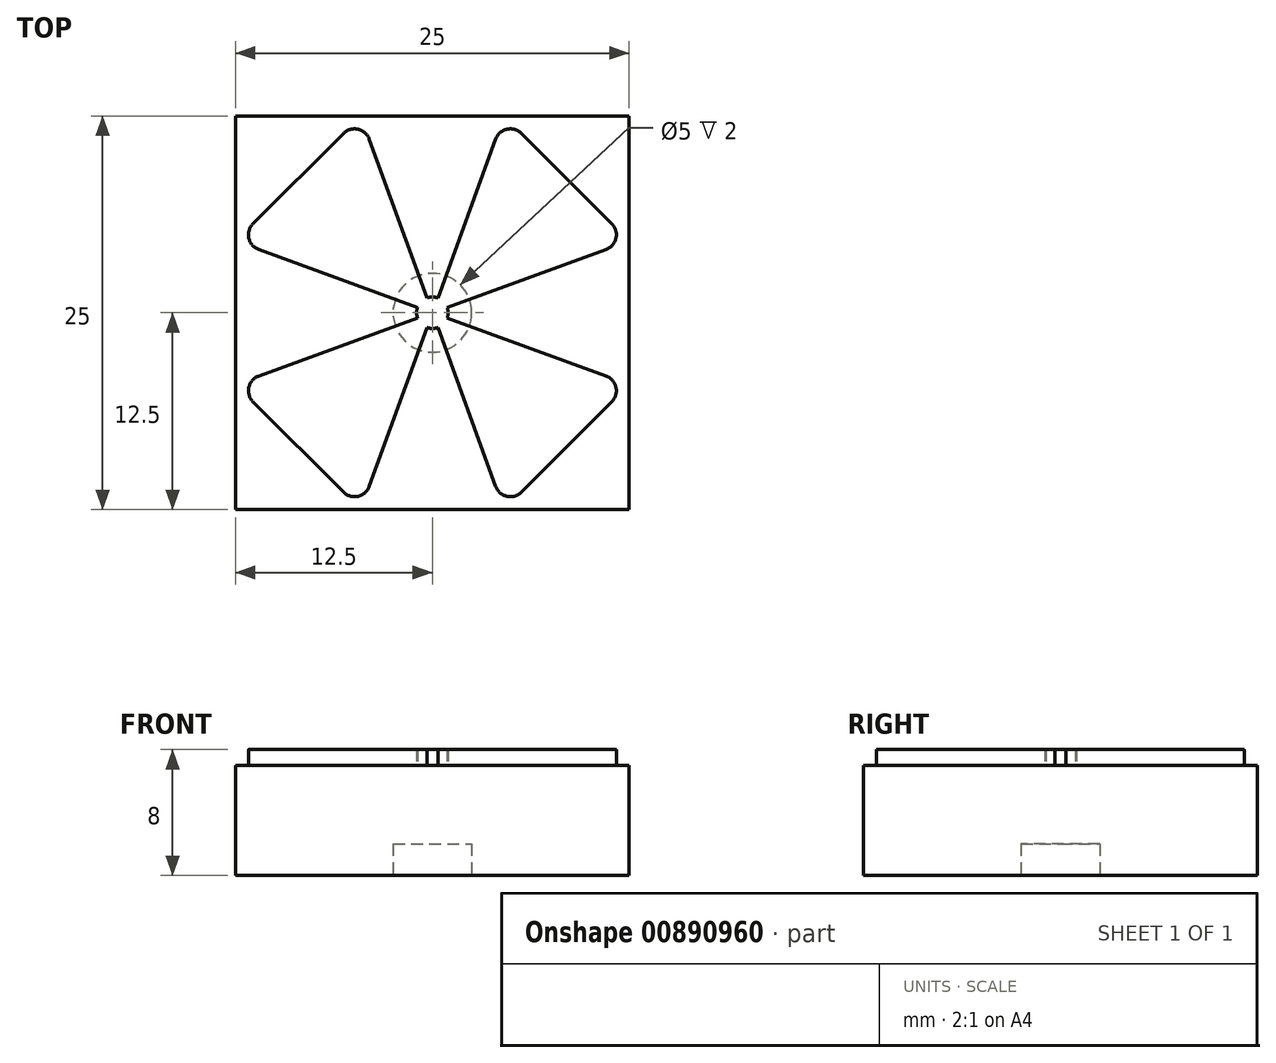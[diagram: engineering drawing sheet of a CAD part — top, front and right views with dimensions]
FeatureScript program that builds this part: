
annotation { "Feature Type Name" : "Feature", "Feature Type Description" : "" }
export const myFeature = defineFeature(function(context is Context, id is Id, definition is map)
    precondition{}
    {
        {
            var Q0;
            Q0=qCreatedBy(makeId("Top.planeOp"),FACE);
            var sketch = newSketch(context, id + "F0", { "sketchPlane" : qUnion([Q0])});
            skLineSegment(sketch, "E0.bottom", {"start": v(-12.5, 12.5) * mm, "end": v(12.5, 12.5) * mm});
            skLineSegment(sketch, "E0.top", {"start": v(-12.5, -12.5) * mm, "end": v(12.5, -12.5) * mm});
            skLineSegment(sketch, "E0.left", {"start": v(-12.5, 12.5) * mm, "end": v(-12.5, -12.5) * mm});
            skLineSegment(sketch, "E0.right", {"start": v(12.5, 12.5) * mm, "end": v(12.5, -12.5) * mm});
            skPoint(sketch, "E0.middle", {"position": v(0, 0) * mm});
            skSolve(sketch);
        }
        {
            var Q0;
            Q0 = qSketchRegion(id + "F0", true);
            extrude(context, id + "F1", {"entities" : qUnion([Q0]), "depth" : 7 * mm, "offsetDistance" : 25 * mm});
        }
        {
            var Q0;
            Q0=makeQuery(id+"F1.opExtrude","CAP_FACE",FACE,{"disambiguationData":[OSD([sQuery(id+"F0.wireOp",EDGE,"E0.bottom"),sQuery(id+"F0.wireOp",EDGE,"E0.top"),sQuery(id+"F0.wireOp",EDGE,"E0.left"),sQuery(id+"F0.wireOp",EDGE,"E0.right")])],"isStart":true});
            var sketch = newSketch(context, id + "F2", { "sketchPlane" : qUnion([Q0])});
            skCircle(sketch, "E1", {"center": v(0, 0) * mm, "radius": 2.5 * mm});
            skSolve(sketch);
        }
        {
            var Q0;
            Q0 = qSketchRegion(id + "F2", true);
            extrude(context, id + "F3", {"entities" : qUnion([Q0]), "operationType" : NewBodyOperationType.REMOVE, "oppositeDirection" : true, "depth" : 2 * mm, "offsetDistance" : 25 * mm});
        }
        {
            var Q0;
            Q0=makeQuery(id+"F1.opExtrude","CAP_FACE",FACE,{"disambiguationData":[OSD([sQuery(id+"F0.wireOp",EDGE,"E0.bottom"),sQuery(id+"F0.wireOp",EDGE,"E0.top"),sQuery(id+"F0.wireOp",EDGE,"E0.left"),sQuery(id+"F0.wireOp",EDGE,"E0.right")])],"isStart":false});
            var sketch = newSketch(context, id + "F4", { "sketchPlane" : qUnion([Q0])});
            skLineSegment(sketch, "E2", {"start": v(-0.94, 0.34) * mm, "end": v(-12.5, 4.55) * mm});
            skLineSegment(sketch, "E3", {"start": v(-12.5, 4.55) * mm, "end": v(-4.55, 12.5) * mm});
            skLineSegment(sketch, "E4", {"start": v(-4.55, 12.5) * mm, "end": v(-0.34, 0.94) * mm});
            skLineSegment(sketch, "E5.MirrorCS", {"start": v(4.55, 12.5) * mm, "end": v(0.34, 0.94) * mm});
            skLineSegment(sketch, "E6.MirrorCS", {"start": v(12.5, 4.55) * mm, "end": v(4.55, 12.5) * mm});
            skLineSegment(sketch, "E7.MirrorCS", {"start": v(0.94, 0.34) * mm, "end": v(12.5, 4.55) * mm});
            skLineSegment(sketch, "E8.MirrorCS", {"start": v(-0.94, -0.34) * mm, "end": v(-12.5, -4.55) * mm});
            skLineSegment(sketch, "E9.MirrorCS", {"start": v(-12.5, -4.55) * mm, "end": v(-4.55, -12.5) * mm});
            skLineSegment(sketch, "E10.MirrorCS", {"start": v(-4.55, -12.5) * mm, "end": v(-0.34, -0.94) * mm});
            skLineSegment(sketch, "E11.MirrorCS", {"start": v(4.55, -12.5) * mm, "end": v(0.34, -0.94) * mm});
            skLineSegment(sketch, "E12.MirrorCS", {"start": v(12.5, -4.55) * mm, "end": v(4.55, -12.5) * mm});
            skLineSegment(sketch, "E13.MirrorCS", {"start": v(0.94, -0.34) * mm, "end": v(12.5, -4.55) * mm});
            skArc(sketch, "E14", {"start": v(0.94, -0.34) * mm, "mid": v(1, 0) * mm, "end": v(0.94, 0.34) * mm});
            skArc(sketch, "E15.trimOffspring", {"start": v(0.34, 0.94) * mm, "mid": v(0, 1) * mm, "end": v(-0.34, 0.94) * mm});
            skArc(sketch, "E16.trimOffspring", {"start": v(-0.94, 0.34) * mm, "mid": v(-1, 0) * mm, "end": v(-0.94, -0.34) * mm});
            skArc(sketch, "E17.trimOffspring", {"start": v(-0.34, -0.94) * mm, "mid": v(0, -1) * mm, "end": v(0.34, -0.94) * mm});
            skSolve(sketch);
        }
        {
            var Q0;
            Q0 = qSketchRegion(id + "F4", true);
            extrude(context, id + "F5", {"entities" : qUnion([Q0]), "operationType" : NewBodyOperationType.ADD, "depth" : 1 * mm, "offsetDistance" : 25 * mm});
        }
        {
            var Q0;
            Q0=makeQuery(id+"F5.opExtrude","SWEPT_EDGE",EDGE,{"disambiguationData":[OSD([sQuery(id+"F0.wireOp",EDGE,"E0.left"),sQuery(id+"F4.wireOp",EDGE,"E2"),sQuery(id+"F4.wireOp",EDGE,"E3")])]});
            var Q1;
            Q1=makeQuery(id+"F5.opExtrude","SWEPT_EDGE",EDGE,{"disambiguationData":[OSD([sQuery(id+"F0.wireOp",EDGE,"E0.bottom"),sQuery(id+"F4.wireOp",EDGE,"E3"),sQuery(id+"F4.wireOp",EDGE,"E4")])]});
            var Q2;
            Q2=makeQuery(id+"F5.opExtrude","SWEPT_EDGE",EDGE,{"disambiguationData":[OSD([sQuery(id+"F0.wireOp",EDGE,"E0.bottom"),sQuery(id+"F4.wireOp",EDGE,"E5.MirrorCS"),sQuery(id+"F4.wireOp",EDGE,"E6.MirrorCS")])]});
            var Q3;
            Q3=makeQuery(id+"F5.opExtrude","SWEPT_EDGE",EDGE,{"disambiguationData":[OSD([sQuery(id+"F0.wireOp",EDGE,"E0.right"),sQuery(id+"F4.wireOp",EDGE,"E6.MirrorCS"),sQuery(id+"F4.wireOp",EDGE,"E7.MirrorCS")])]});
            var Q4;
            Q4=makeQuery(id+"F5.opExtrude","SWEPT_EDGE",EDGE,{"disambiguationData":[OSD([sQuery(id+"F0.wireOp",EDGE,"E0.top"),sQuery(id+"F4.wireOp",EDGE,"E11.MirrorCS"),sQuery(id+"F4.wireOp",EDGE,"E12.MirrorCS")])]});
            var Q5;
            Q5=makeQuery(id+"F5.opExtrude","SWEPT_EDGE",EDGE,{"disambiguationData":[OSD([sQuery(id+"F0.wireOp",EDGE,"E0.right"),sQuery(id+"F4.wireOp",EDGE,"E12.MirrorCS"),sQuery(id+"F4.wireOp",EDGE,"E13.MirrorCS")])]});
            var Q6;
            Q6=makeQuery(id+"F5.opExtrude","SWEPT_EDGE",EDGE,{"disambiguationData":[OSD([sQuery(id+"F0.wireOp",EDGE,"E0.top"),sQuery(id+"F4.wireOp",EDGE,"E9.MirrorCS"),sQuery(id+"F4.wireOp",EDGE,"E10.MirrorCS")])]});
            var Q7;
            Q7=makeQuery(id+"F5.opExtrude","SWEPT_EDGE",EDGE,{"disambiguationData":[OSD([sQuery(id+"F0.wireOp",EDGE,"E0.left"),sQuery(id+"F4.wireOp",EDGE,"E8.MirrorCS"),sQuery(id+"F4.wireOp",EDGE,"E9.MirrorCS")])]});
            fillet(context, id + "F6", {"entities" : qUnion([Q0, Q1, Q2, Q3, Q4, Q5, Q6, Q7]), "radius" : 1 * mm, "tangentPropagation" : true, "allowEdgeOverflow" : false});
        }
    });
